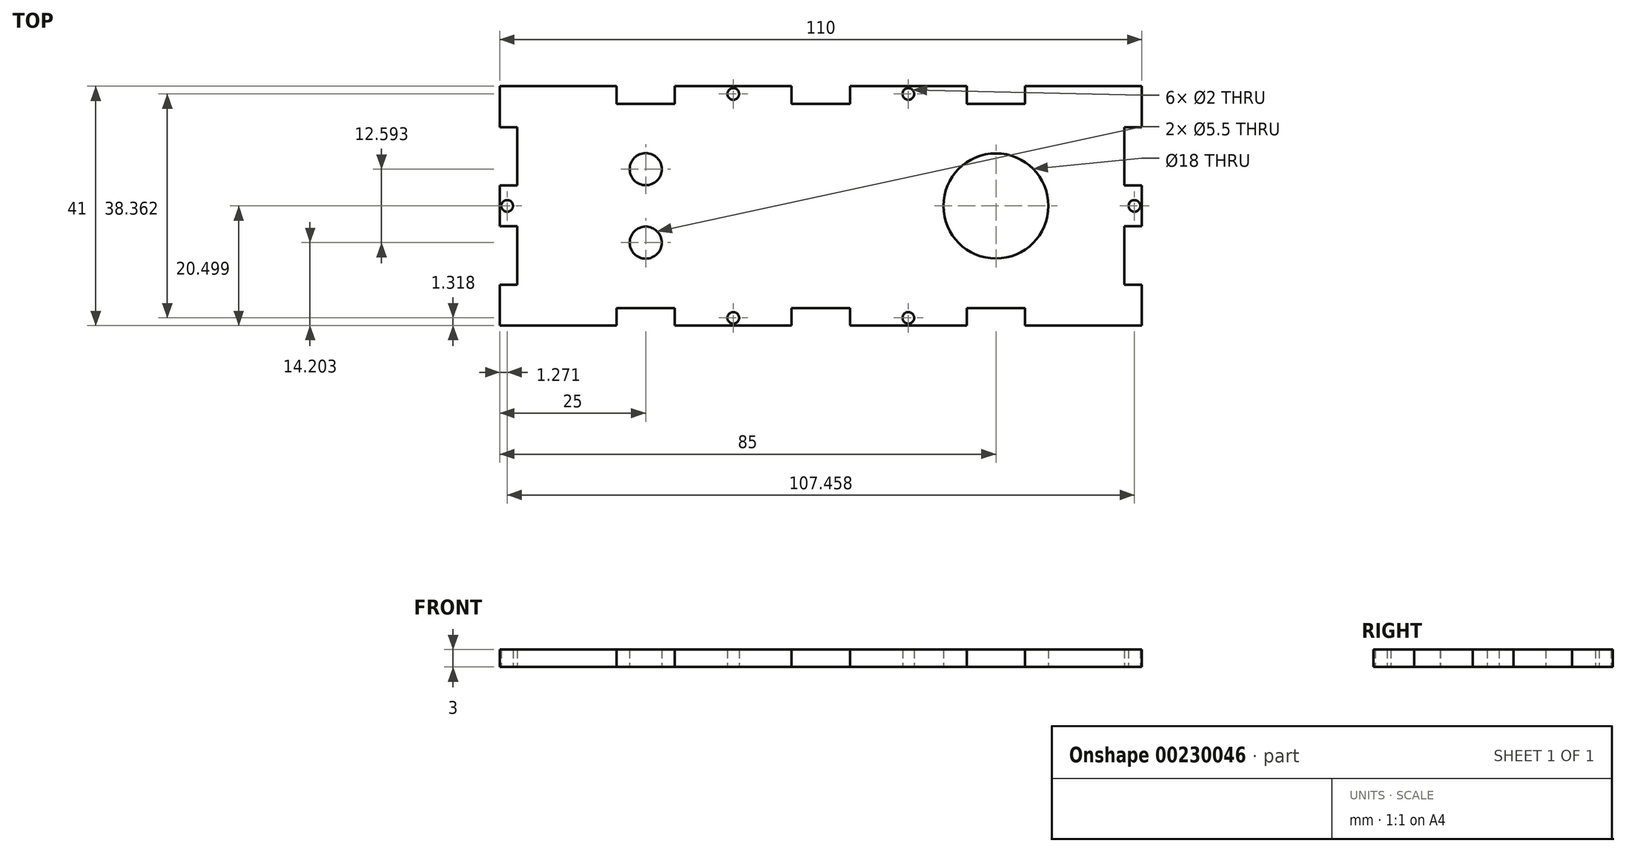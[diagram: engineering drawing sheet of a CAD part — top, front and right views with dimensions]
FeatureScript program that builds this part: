
annotation { "Feature Type Name" : "Feature", "Feature Type Description" : "" }
export const myFeature = defineFeature(function(context is Context, id is Id, definition is map)
    precondition{}
    {
        {
            var Q0;
            Q0=qCreatedBy(makeId("Top.planeOp"),FACE);
            var sketch = newSketch(context, id + "F0", { "sketchPlane" : qUnion([Q0])});
            skLineSegment(sketch, "E0", {"start": v(-48.75, -11.5) * mm, "end": v(-48.75, -4.5) * mm});
            skLineSegment(sketch, "E1", {"start": v(-48.75, -4.5) * mm, "end": v(-45.75, -4.5) * mm});
            skLineSegment(sketch, "E2", {"start": v(-45.75, -4.5) * mm, "end": v(-45.75, 5.5) * mm});
            skLineSegment(sketch, "E3", {"start": v(-45.75, 5.5) * mm, "end": v(-48.75, 5.5) * mm});
            skLineSegment(sketch, "E4", {"start": v(-48.75, 5.5) * mm, "end": v(-48.75, 12.5) * mm});
            skLineSegment(sketch, "E5", {"start": v(-48.75, 12.5) * mm, "end": v(-45.75, 12.5) * mm});
            skLineSegment(sketch, "E6", {"start": v(-45.75, 12.5) * mm, "end": v(-45.75, 22.5) * mm});
            skLineSegment(sketch, "E7", {"start": v(-45.75, 22.5) * mm, "end": v(-48.75, 22.5) * mm});
            skLineSegment(sketch, "E8", {"start": v(-48.75, 22.5) * mm, "end": v(-48.75, 29.5) * mm});
            skLineSegment(sketch, "E9", {"start": v(-48.75, 29.5) * mm, "end": v(-28.75, 29.5) * mm});
            skLineSegment(sketch, "E10", {"start": v(-28.75, 29.5) * mm, "end": v(-28.75, 26.5) * mm});
            skLineSegment(sketch, "E11", {"start": v(-28.75, 26.5) * mm, "end": v(-18.75, 26.5) * mm});
            skLineSegment(sketch, "E12", {"start": v(-18.75, 26.5) * mm, "end": v(-18.75, 29.5) * mm});
            skLineSegment(sketch, "E13", {"start": v(-18.75, 29.5) * mm, "end": v(1.25, 29.5) * mm});
            skLineSegment(sketch, "E14", {"start": v(1.25, 29.5) * mm, "end": v(1.25, 26.5) * mm});
            skLineSegment(sketch, "E15", {"start": v(1.25, 26.5) * mm, "end": v(6.25, 26.5) * mm});
            skLineSegment(sketch, "E16", {"start": v(6.25, 26.5) * mm, "end": v(6.25, -11.5) * mm, "construction": true});
            skLineSegment(sketch, "E17", {"start": v(-48.75, 9) * mm, "end": v(6.25, 9) * mm, "construction": true});
            skLineSegment(sketch, "E18.MirrorCS", {"start": v(1.25, -8.5) * mm, "end": v(6.25, -8.5) * mm});
            skLineSegment(sketch, "E19.MirrorCS", {"start": v(1.25, -11.5) * mm, "end": v(1.25, -8.5) * mm});
            skLineSegment(sketch, "E20.MirrorCS", {"start": v(-18.75, -8.5) * mm, "end": v(-18.75, -11.5) * mm});
            skLineSegment(sketch, "E21.MirrorCS", {"start": v(-45.75, -4.5) * mm, "end": v(-48.75, -4.5) * mm});
            skLineSegment(sketch, "E22.MirrorCS", {"start": v(-48.75, 5.5) * mm, "end": v(-45.75, 5.5) * mm});
            skLineSegment(sketch, "E23.MirrorCS", {"start": v(-28.75, -11.5) * mm, "end": v(-28.75, -8.5) * mm});
            skLineSegment(sketch, "E24.MirrorCS", {"start": v(-18.75, -11.5) * mm, "end": v(1.25, -11.5) * mm});
            skLineSegment(sketch, "E25.MirrorCS", {"start": v(-28.75, -8.5) * mm, "end": v(-18.75, -8.5) * mm});
            skLineSegment(sketch, "E26.MirrorCS", {"start": v(-45.75, 5.5) * mm, "end": v(-45.75, -4.5) * mm});
            skLineSegment(sketch, "E27.MirrorCS", {"start": v(-48.75, -4.5) * mm, "end": v(-48.75, -11.5) * mm});
            skLineSegment(sketch, "E28.MirrorCS", {"start": v(-48.75, -11.5) * mm, "end": v(-28.75, -11.5) * mm});
            skLineSegment(sketch, "E29.MirrorCS", {"start": v(58.25, -4.5) * mm, "end": v(61.25, -4.5) * mm});
            skLineSegment(sketch, "E30.MirrorCS", {"start": v(61.25, -4.5) * mm, "end": v(58.25, -4.5) * mm});
            skLineSegment(sketch, "E31.MirrorCS", {"start": v(58.25, 5.5) * mm, "end": v(61.25, 5.5) * mm});
            skLineSegment(sketch, "E32.MirrorCS", {"start": v(61.25, 5.5) * mm, "end": v(58.25, 5.5) * mm});
            skLineSegment(sketch, "E33.MirrorCS", {"start": v(61.25, 5.5) * mm, "end": v(61.25, 12.5) * mm});
            skLineSegment(sketch, "E34.MirrorCS", {"start": v(31.25, -8.5) * mm, "end": v(31.25, -11.5) * mm});
            skLineSegment(sketch, "E35.MirrorCS", {"start": v(41.25, -11.5) * mm, "end": v(41.25, -8.5) * mm});
            skLineSegment(sketch, "E36.MirrorCS", {"start": v(31.25, 26.5) * mm, "end": v(31.25, 29.5) * mm});
            skLineSegment(sketch, "E37.MirrorCS", {"start": v(41.25, 29.5) * mm, "end": v(41.25, 26.5) * mm});
            skLineSegment(sketch, "E38.MirrorCS", {"start": v(58.25, 22.5) * mm, "end": v(61.25, 22.5) * mm});
            skLineSegment(sketch, "E39.MirrorCS", {"start": v(61.25, 12.5) * mm, "end": v(58.25, 12.5) * mm});
            skLineSegment(sketch, "E40.MirrorCS", {"start": v(11.25, 29.5) * mm, "end": v(11.25, 26.5) * mm});
            skLineSegment(sketch, "E41.MirrorCS", {"start": v(58.25, 5.5) * mm, "end": v(58.25, -4.5) * mm});
            skLineSegment(sketch, "E42.MirrorCS", {"start": v(11.25, -11.5) * mm, "end": v(11.25, -8.5) * mm});
            skLineSegment(sketch, "E43.MirrorCS", {"start": v(61.25, -11.5) * mm, "end": v(61.25, -4.5) * mm});
            skLineSegment(sketch, "E44.MirrorCS", {"start": v(58.25, -4.5) * mm, "end": v(58.25, 5.5) * mm});
            skLineSegment(sketch, "E45.MirrorCS", {"start": v(11.25, -8.5) * mm, "end": v(6.25, -8.5) * mm});
            skLineSegment(sketch, "E46.MirrorCS", {"start": v(41.25, -8.5) * mm, "end": v(31.25, -8.5) * mm});
            skLineSegment(sketch, "E47.MirrorCS", {"start": v(61.25, -4.5) * mm, "end": v(61.25, -11.5) * mm});
            skLineSegment(sketch, "E48.MirrorCS", {"start": v(41.25, 26.5) * mm, "end": v(31.25, 26.5) * mm});
            skLineSegment(sketch, "E49.MirrorCS", {"start": v(61.25, 29.5) * mm, "end": v(41.25, 29.5) * mm});
            skLineSegment(sketch, "E50.MirrorCS", {"start": v(61.25, 22.5) * mm, "end": v(61.25, 29.5) * mm});
            skLineSegment(sketch, "E51.MirrorCS", {"start": v(58.25, 12.5) * mm, "end": v(58.25, 22.5) * mm});
            skLineSegment(sketch, "E52.MirrorCS", {"start": v(11.25, 26.5) * mm, "end": v(6.25, 26.5) * mm});
            skLineSegment(sketch, "E53.MirrorCS", {"start": v(61.25, 9) * mm, "end": v(6.25, 9) * mm, "construction": true});
            skLineSegment(sketch, "E54.MirrorCS", {"start": v(31.25, 29.5) * mm, "end": v(11.25, 29.5) * mm});
            skLineSegment(sketch, "E55.MirrorCS", {"start": v(31.25, -11.5) * mm, "end": v(11.25, -11.5) * mm});
            skLineSegment(sketch, "E56.MirrorCS", {"start": v(61.25, -11.5) * mm, "end": v(41.25, -11.5) * mm});
            skCircle(sketch, "E57", {"center": v(-47.48, 9) * mm, "radius": 1 * mm});
            skPoint(sketch, "E58", {"position": v(-8.75, -11.5) * mm});
            skCircle(sketch, "E59", {"center": v(-8.75, -10.18) * mm, "radius": 1 * mm});
            skCircle(sketch, "E60.MirrorC", {"center": v(59.98, 9) * mm, "radius": 1 * mm});
            skCircle(sketch, "E61.MirrorC", {"center": v(21.25, -10.18) * mm, "radius": 1 * mm});
            skCircle(sketch, "E62.MirrorC", {"center": v(-8.75, 28.18) * mm, "radius": 1 * mm});
            skCircle(sketch, "E63.MirrorC", {"center": v(21.25, 28.18) * mm, "radius": 1 * mm});
            skPoint(sketch, "E64", {"position": v(-23.75, 26.5) * mm});
            skPoint(sketch, "E65", {"position": v(-23.75, -8.5) * mm});
            skCircle(sketch, "E66", {"center": v(-23.75, 2.7) * mm, "radius": 2.75 * mm});
            skCircle(sketch, "E67.MirrorC", {"center": v(-23.75, 15.3) * mm, "radius": 2.75 * mm});
            skPoint(sketch, "E68", {"position": v(36.25, 26.5) * mm});
            skCircle(sketch, "E69", {"center": v(36.25, 9) * mm, "radius": 9 * mm});
            skSolve(sketch);
        }
        {
            var Q0;
            Q0=makeQuery(id+"F0.imprint","IMPRINT",FACE,{"disambiguationData":[TD([[makeQuery(id+"F0.imprint","IMPRINT",EDGE,{"derivedFrom":sQuery(id+"F0.wireOp",EDGE,"E4")}),-1.0]])]});
            extrude(context, id + "F1", {"entities" : qUnion([Q0]), "depth" : 3 * mm});
        }
    });
